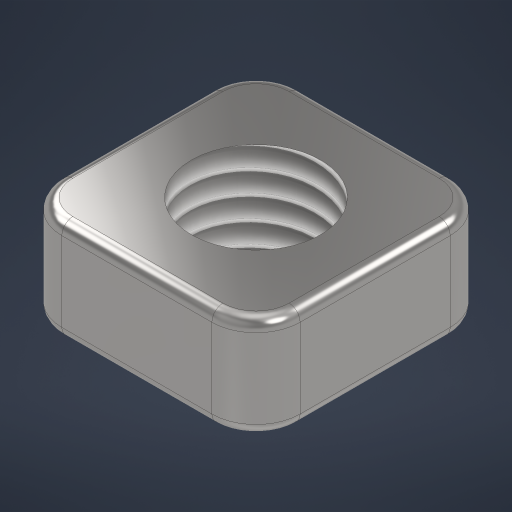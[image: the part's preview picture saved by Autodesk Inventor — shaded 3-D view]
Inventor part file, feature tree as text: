
AUTODESK INVENTOR PART (.ipt)
format: ipt  version: 2024 (Build 280153000, 153)  size: 257,024 bytes
history: native  units: mm
features: extrude x1, fillet x1, thread x1, sketch x1
ambient origin geometry x8: Origin, YZ Plane, XZ Plane, XY Plane, X Axis, Y Axis, Z Axis, Center Point
bodies: Solid1 (feature_tree)
feature tree (4):
  extrude  "Extrusion1"  Depth=5.4mm
  fillet  "Fillet1"  Radius=5.4mm
  thread  "Thread1"  [1 undecoded]
  sketch  "Sketch1"  dims[d0=2.93mm d1=5.4mm d2=5.4mm d3=1.0mm d4=2.3mm d5=0.0mm d6=0.25mm d7=2.3mm d8=0.0mm]
note: 1 required parameter value undecoded (feature->parameter linkage not recoverable at this tier; creation-order binding heuristic only, values carry confidence <= 0.55)
